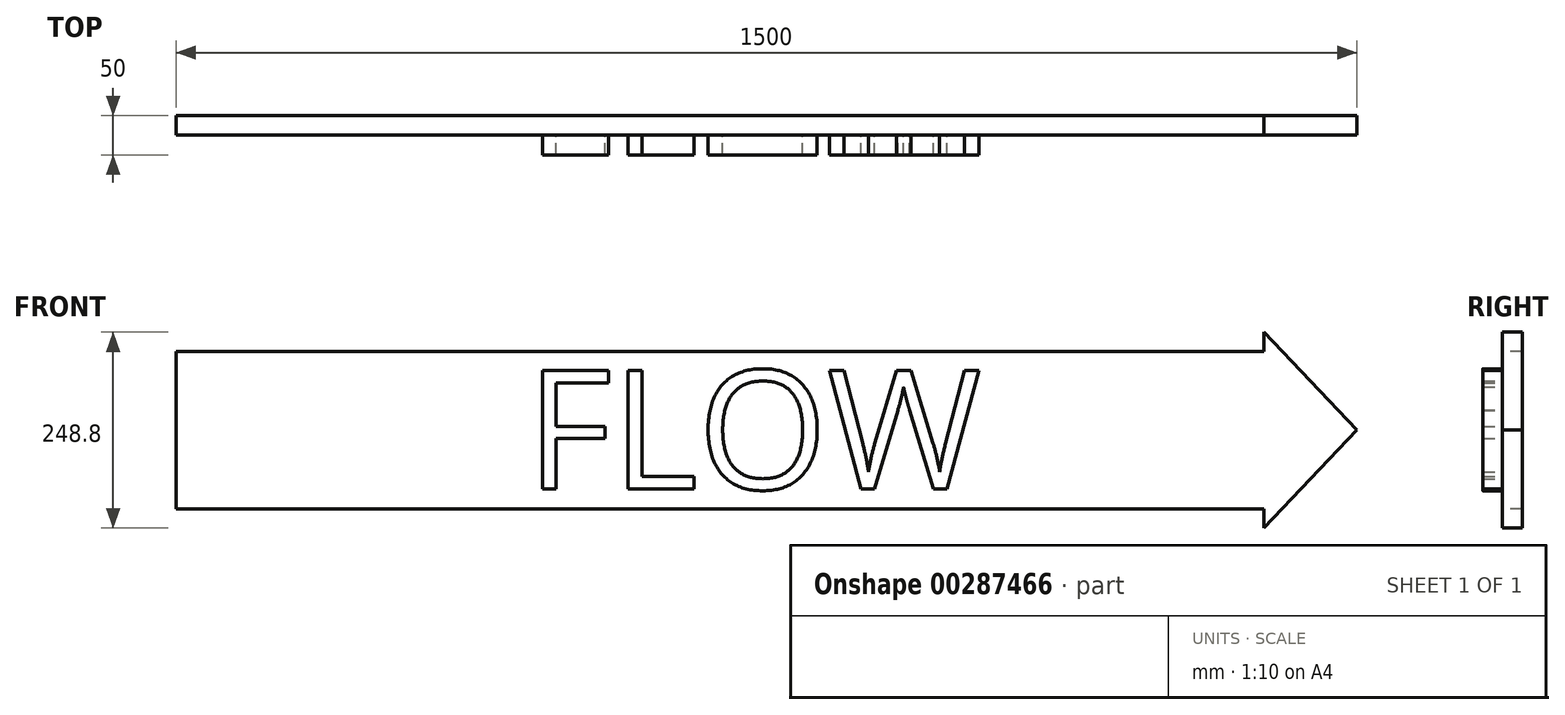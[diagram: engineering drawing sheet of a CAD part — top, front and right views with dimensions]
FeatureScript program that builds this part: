
annotation { "Feature Type Name" : "Feature", "Feature Type Description" : "" }
export const myFeature = defineFeature(function(context is Context, id is Id, definition is map)
    precondition{}
    {
        {
            var Q0;
            Q0=qCreatedBy(makeId("Front.planeOp"),FACE);
            var sketch = newSketch(context, id + "F0", { "sketchPlane" : qUnion([Q0])});
            skLineSegment(sketch, "E0", {"start": v(0, 0) * mm, "end": v(0, 100) * mm});
            skLineSegment(sketch, "E1", {"start": v(0, 100) * mm, "end": v(1381.62, 100) * mm});
            skLineSegment(sketch, "E2", {"start": v(1381.62, 100) * mm, "end": v(1381.62, 124.4) * mm});
            skLineSegment(sketch, "E3", {"start": v(1381.62, 124.4) * mm, "end": v(1500, 0) * mm});
            skLineSegment(sketch, "E4", {"start": v(1500, 0) * mm, "end": v(0, 0) * mm});
            skLineSegment(sketch, "E5.MirrorCS", {"start": v(0, 0) * mm, "end": v(0, -100) * mm});
            skLineSegment(sketch, "E6.MirrorCS", {"start": v(0, -100) * mm, "end": v(1381.62, -100) * mm});
            skLineSegment(sketch, "E7.MirrorCS", {"start": v(1381.62, -100) * mm, "end": v(1381.62, -124.4) * mm});
            skLineSegment(sketch, "E8.MirrorCS", {"start": v(1381.62, -124.4) * mm, "end": v(1500, 0) * mm});
            skSolve(sketch);
        }
        {
            var Q0;
            Q0=qSketchRegion(id+"F0",true);
            extrude(context, id + "F1", {"entities" : qUnion([Q0]), "oppositeDirection" : true, "depth" : 25 * mm});
        }
        {
            var Q0;
            Q0=qCreatedBy(makeId("Front.planeOp"),FACE);
            var sketch = newSketch(context, id + "F2", { "sketchPlane" : qUnion([Q0])});
            skText(sketch, "E9", { "text": "FLOW", "fontName": "OpenSans-Regular.ttf"});
            const initialGuessF2  = {"E9": [0.4446, -0.07517, 1, 0, 0.15191]};
            skSetInitialGuess(sketch, initialGuessF2);
            skSolve(sketch);
        }
        {
            var Q0;
            Q0=qSketchRegion(id+"F2",true);
            extrude(context, id + "F3", {"entities" : qUnion([Q0]), "operationType" : NewBodyOperationType.ADD, "depth" : 25 * mm});
        }
    });
